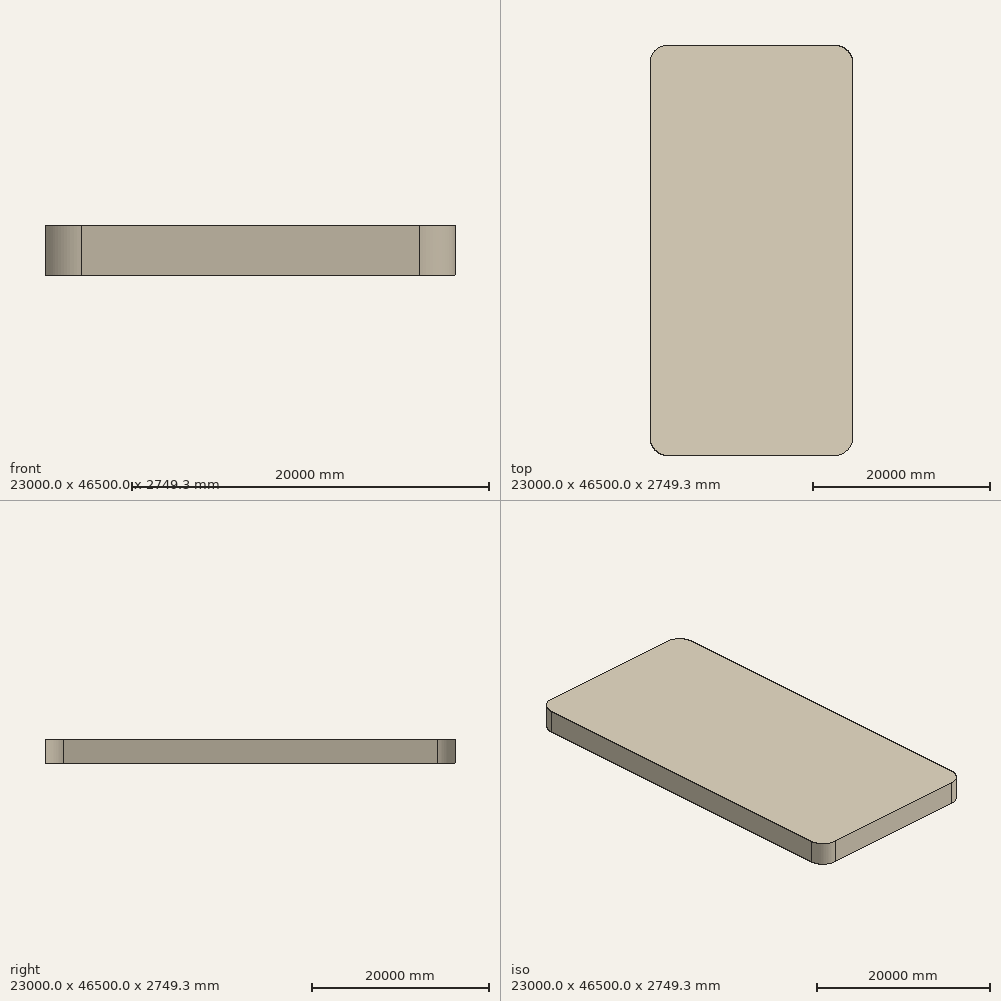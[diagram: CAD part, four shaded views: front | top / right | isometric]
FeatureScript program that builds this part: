
annotation { "Feature Type Name" : "Feature", "Feature Type Description" : "" }
export const myFeature = defineFeature(function(context is Context, id is Id, definition is map)
    precondition{}
    {
        {
            var Q0;
            Q0=qCreatedBy(makeId("Top.planeOp"),FACE);
            var sketch = newSketch(context, id + "F0", { "sketchPlane" : qUnion([Q0])});
            skLineSegment(sketch, "E0", {"start": v(0, 0) * mm, "end": v(0, -46500) * mm});
            skLineSegment(sketch, "E1", {"start": v(0, -46500) * mm, "end": v(23000, -46500) * mm});
            skLineSegment(sketch, "E2", {"start": v(23000, -46500) * mm, "end": v(23000, 0) * mm});
            skLineSegment(sketch, "E3", {"start": v(23000, 0) * mm, "end": v(0, 0) * mm});
            skSolve(sketch);
        }
        {
            var Q0;
            Q0=makeQuery(id+"F0.imprint","IMPRINT",FACE,{"disambiguationData":[TD([[makeQuery(id+"F0.imprint","IMPRINT",EDGE,{"derivedFrom":sQuery(id+"F0.wireOp",EDGE,"E0")}),1.0]])]});
            extrude(context, id + "F1", {"entities" : qUnion([Q0]), "depth" : 2749.3 * mm});
        }
        {
            var Q0;
            Q0=makeQuery(id+"F1.opExtrude","SWEPT_EDGE",EDGE,{"disambiguationData":[OSD([sQuery(id+"F0.wireOp",EDGE,"E1"),sQuery(id+"F0.wireOp",EDGE,"E2")])]});
            var Q1;
            Q1=makeQuery(id+"F1.opExtrude","SWEPT_EDGE",EDGE,{"disambiguationData":[OSD([sQuery(id+"F0.wireOp",EDGE,"E0"),sQuery(id+"F0.wireOp",EDGE,"E1")])]});
            var Q2;
            Q2=makeQuery(id+"F1.opExtrude","SWEPT_EDGE",EDGE,{"disambiguationData":[OSD([sQuery(id+"F0.wireOp",EDGE,"E2"),sQuery(id+"F0.wireOp",EDGE,"E3")])]});
            var Q3;
            Q3=makeQuery(id+"F1.opExtrude","SWEPT_EDGE",EDGE,{"disambiguationData":[OSD([sQuery(id+"F0.wireOp",EDGE,"E0"),sQuery(id+"F0.wireOp",EDGE,"E3")])]});
            fillet(context, id + "F2", {"entities" : qUnion([Q0, Q1, Q2, Q3]), "radius" : 2000 * mm, "tangentPropagation" : true, "allowEdgeOverflow" : false});
        }
    });
